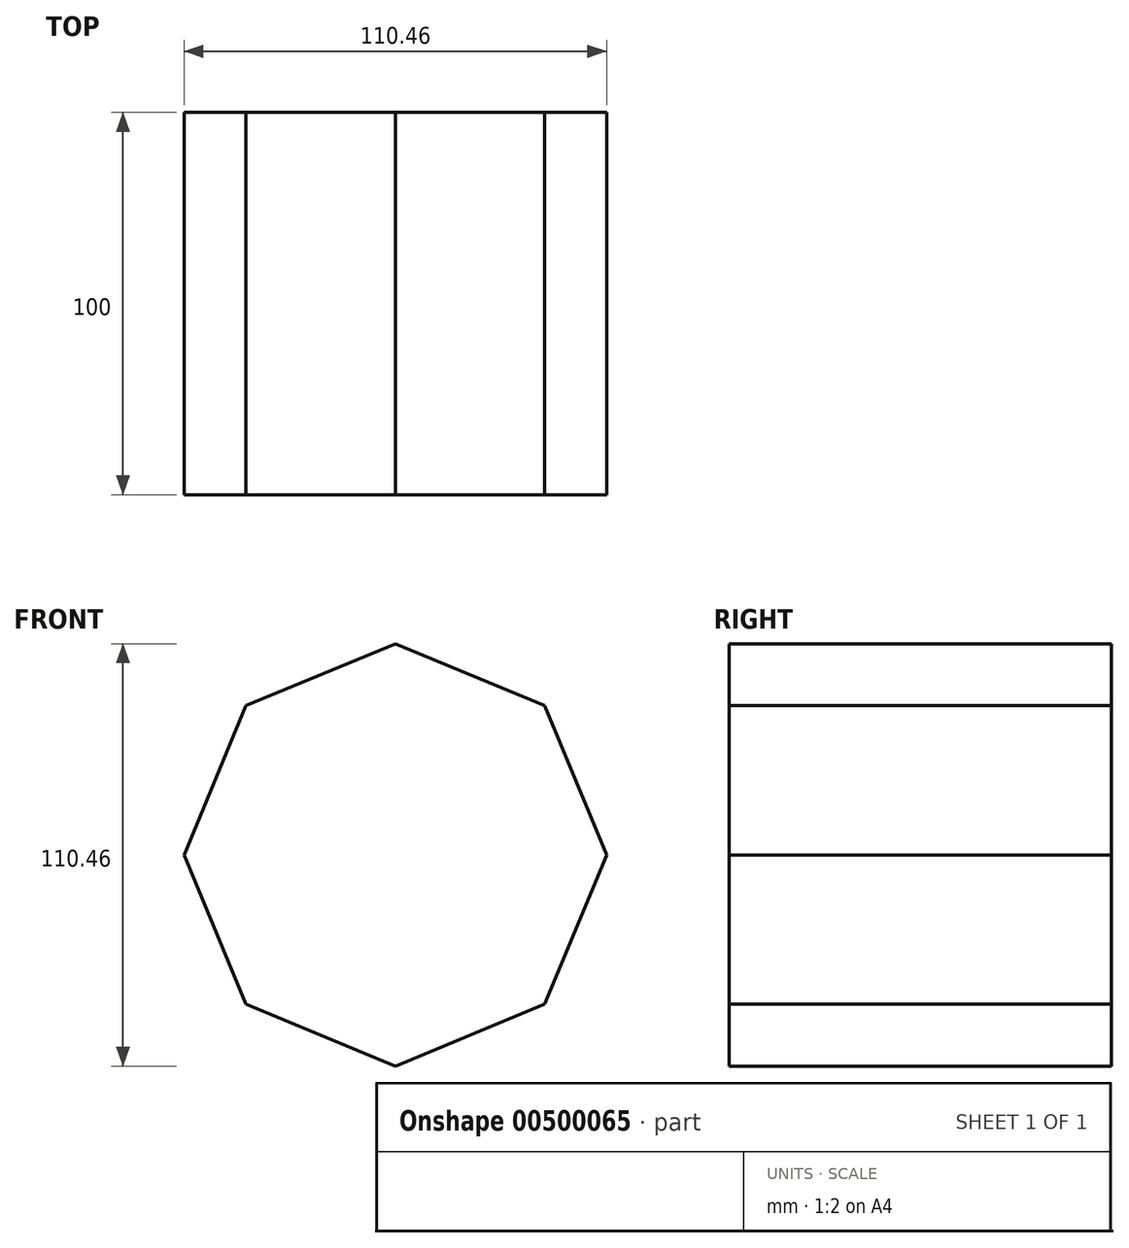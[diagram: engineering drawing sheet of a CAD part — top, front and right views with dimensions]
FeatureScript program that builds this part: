
annotation { "Feature Type Name" : "Feature", "Feature Type Description" : "" }
export const myFeature = defineFeature(function(context is Context, id is Id, definition is map)
    precondition{}
    {
        {
            var Q0;
            Q0=qCreatedBy(makeId("Front.planeOp"),FACE);
            var sketch = newSketch(context, id + "F0", { "sketchPlane" : qUnion([Q0])});
            skCircle(sketch, "E0.cCircle", {"center": v(0, 0) * mm, "radius": 55.23 * mm, "construction": true});
            skLineSegment(sketch, "E0.0", {"start": v(0, 55.23) * mm, "end": v(39.06, 39.06) * mm});
            skLineSegment(sketch, "E0.1", {"start": v(39.06, 39.06) * mm, "end": v(55.23, 0) * mm});
            skLineSegment(sketch, "E0.2", {"start": v(55.23, 0) * mm, "end": v(39.06, -39.06) * mm});
            skLineSegment(sketch, "E0.3", {"start": v(39.06, -39.06) * mm, "end": v(0, -55.23) * mm});
            skLineSegment(sketch, "E0.4", {"start": v(0, -55.23) * mm, "end": v(-39.06, -39.06) * mm});
            skLineSegment(sketch, "E0.5", {"start": v(-39.06, -39.06) * mm, "end": v(-55.23, 0) * mm});
            skLineSegment(sketch, "E0.6", {"start": v(-55.23, 0) * mm, "end": v(-39.06, 39.06) * mm});
            skLineSegment(sketch, "E0.7", {"start": v(-39.06, 39.06) * mm, "end": v(0, 55.23) * mm});
            skSolve(sketch);
        }
        {
            var Q0;
            Q0=makeQuery(id+"F0.imprint","IMPRINT",FACE,{"disambiguationData":[TD([[makeQuery(id+"F0.imprint","IMPRINT",EDGE,{"derivedFrom":sQuery(id+"F0.wireOp",EDGE,"E0.0")}),-1.0]])]});
            extrude(context, id + "F1", {"entities" : qUnion([Q0]), "depth" : 100 * mm, "symmetric" : true});
        }
    });
